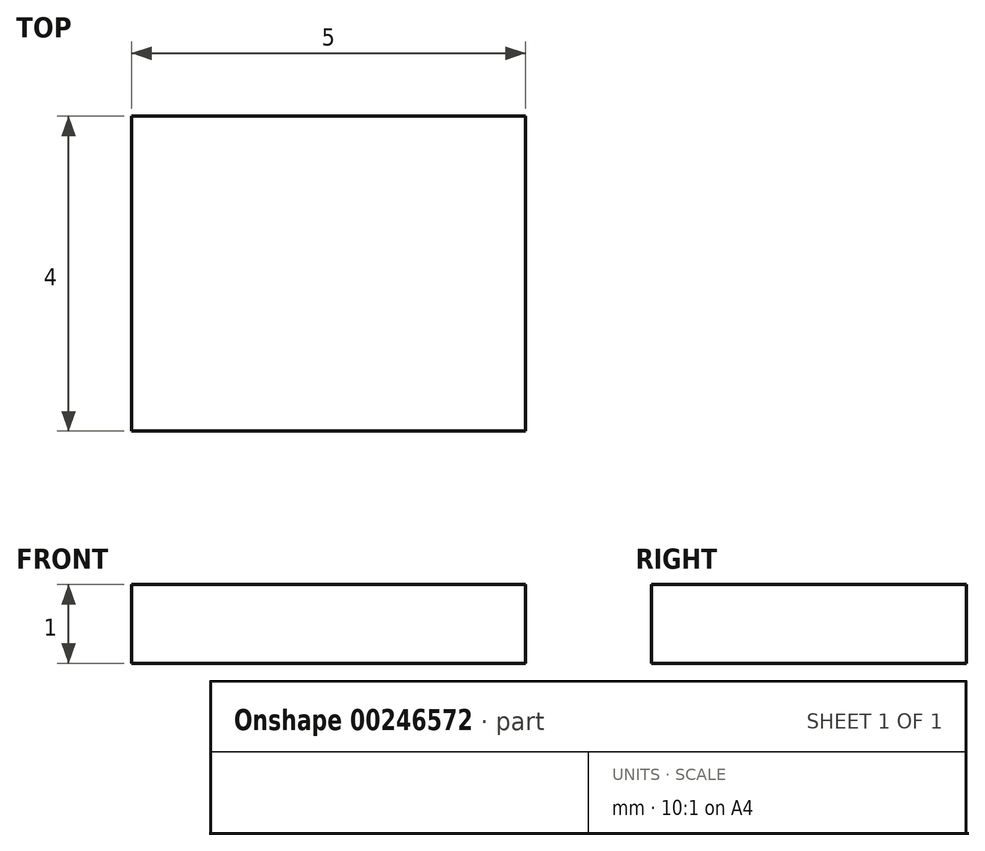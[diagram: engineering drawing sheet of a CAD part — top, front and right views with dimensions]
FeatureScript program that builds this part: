
annotation { "Feature Type Name" : "Feature", "Feature Type Description" : "" }
export const myFeature = defineFeature(function(context is Context, id is Id, definition is map)
    precondition{}
    {
        {
            var Q0;
            Q0=qCreatedBy(makeId("Top.planeOp"),FACE);
            var sketch = newSketch(context, id + "F0", { "sketchPlane" : qUnion([Q0])});
            skLineSegment(sketch, "E0.bottom", {"start": v(0, 0) * mm, "end": v(5, 0) * mm});
            skLineSegment(sketch, "E0.top", {"start": v(0, 4) * mm, "end": v(5, 4) * mm});
            skLineSegment(sketch, "E0.left", {"start": v(0, 0) * mm, "end": v(0, 4) * mm});
            skLineSegment(sketch, "E0.right", {"start": v(5, 0) * mm, "end": v(5, 4) * mm});
            skSolve(sketch);
        }
        {
            var Q0;
            Q0=makeQuery(id+"F0.imprint","IMPRINT",FACE,{"disambiguationData":[TD([[makeQuery(id+"F0.imprint","IMPRINT",EDGE,{"derivedFrom":sQuery(id+"F0.wireOp",EDGE,"E0.bottom")}),1.0]])]});
            extrude(context, id + "F1", {"entities" : qUnion([Q0]), "depth" : 1 * mm});
        }
    });
